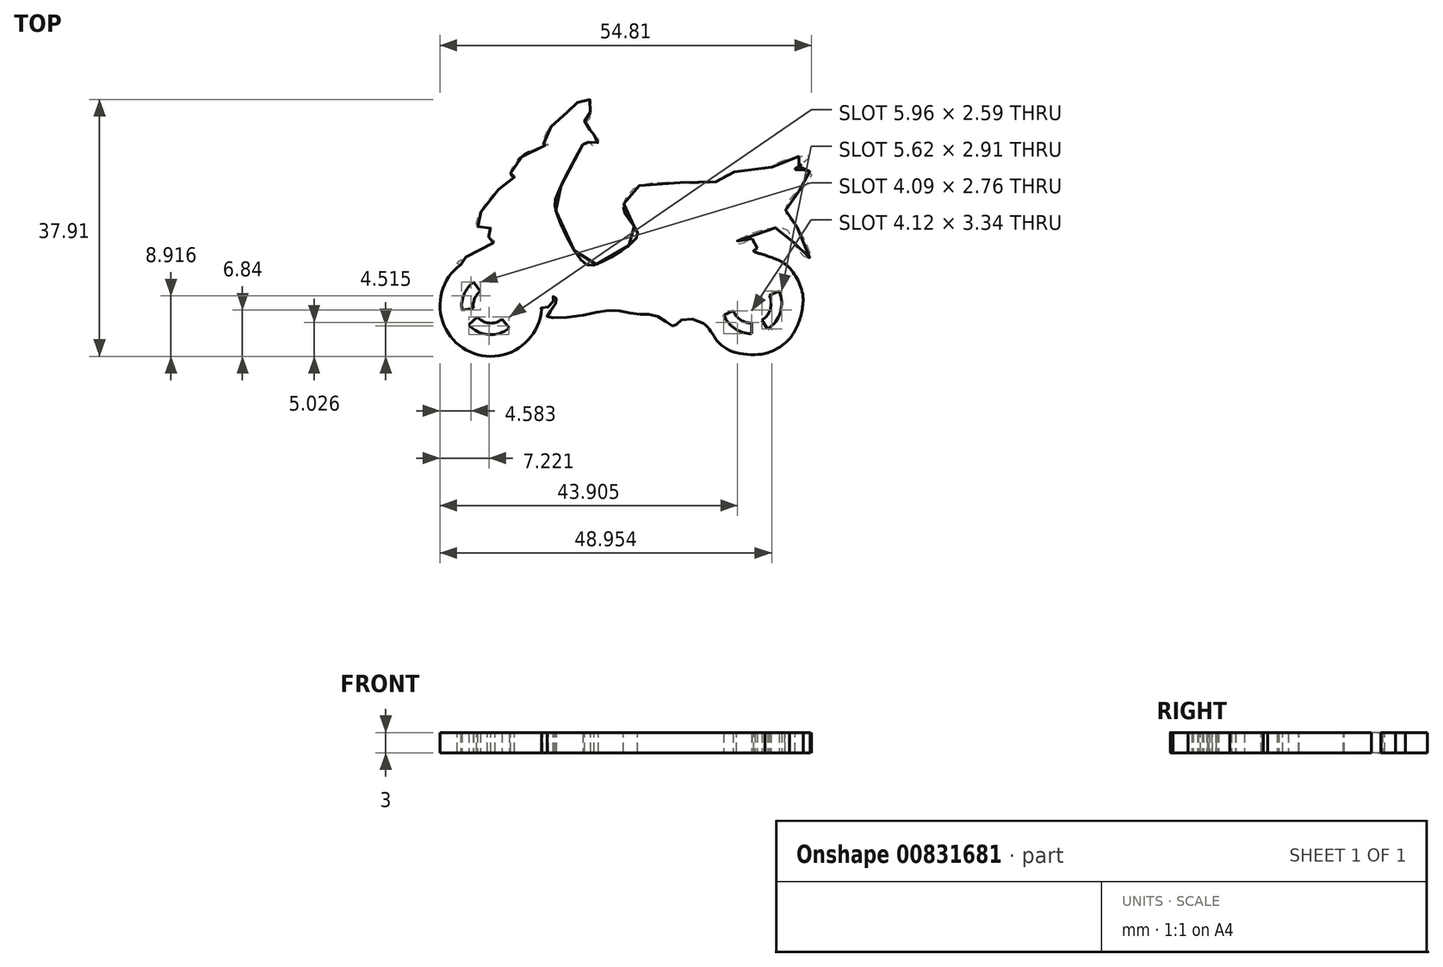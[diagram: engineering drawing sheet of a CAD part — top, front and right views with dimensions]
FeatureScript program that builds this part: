
annotation { "Feature Type Name" : "Feature", "Feature Type Description" : "" }
export const myFeature = defineFeature(function(context is Context, id is Id, definition is map)
    precondition{}
    {
        {
            var Q0;
            Q0=qCreatedBy(makeId("Top.planeOp"),FACE);
            var sketch = newSketch(context, id + "F0", { "sketchPlane" : qUnion([Q0])});
            skFitSpline(sketch, "E0", {"points": [v(13.76, 24.36) * mm, v(9.91, 16.67) * mm, v(9.86, 14.36) * mm, v(13.76, 6.98) * mm, v(15.97, 6.72) * mm, v(21.34, 10.1) * mm, v(21.76, 11.56) * mm, v(19.92, 14.3) * mm, v(20.18, 16.46) * mm, v(22.6, 18.41) * mm, v(30.77, 18.57) * mm, v(34.14, 19.15) * mm, v(35.35, 20.1) * mm, v(41.67, 20.94) * mm, v(42.09, 21.41) * mm, v(47.3, 22.57) * mm, v(45.14, 20.73) * mm, v(45.14, 20.62) * mm, v(47.35, 20.25) * mm, v(46.4, 17.99) * mm, v(44.25, 16.25) * mm, v(43.72, 13.99) * mm, v(44.83, 12.83) * mm, v(47.3, 7.83) * mm, v(46.83, 7.46) * mm, v(44.67, 10.3) * mm, v(43.2, 12.04) * mm, v(36.5, 10.04) * mm, v(36.61, 9.62) * mm, v(38.98, 10.56) * mm], "startDerivative": vector(-82.9, -156.15) * mm, "endDerivative": vector(91.63, 50.65) * mm});
            skFitSpline(sketch, "E1", {"points": [v(-4.24, 6.58) * mm, v(-4.76, 6.84) * mm, v(0.82, 9.98) * mm, v(0.55, 10.1) * mm, v(-0.29, 11.19) * mm, v(0.18, 11.91) * mm, v(-1.32, 12.04) * mm, v(-1.9, 12.64) * mm, v(1, 17.35) * mm, v(3.72, 19.55) * mm, v(3.5, 19.62) * mm, v(3.12, 19.93) * mm, v(5.41, 22.97) * mm, v(8.7, 24.31) * mm, v(8, 24.47) * mm, v(9.6, 27.5) * mm, v(12.35, 29.78) * mm, v(13.26, 30.69) * mm, v(14.86, 30.9) * mm, v(14.89, 30.5) * mm, v(14.54, 27.78) * mm, v(14.04, 27.74) * mm, v(14.2, 27.59) * mm, v(14.95, 26.34) * mm, v(15.42, 26.24) * mm, v(15.51, 25.55) * mm, v(16.05, 25.05) * mm, v(15.42, 24.11) * mm, v(14.57, 24.68) * mm, v(14.39, 24.36) * mm, v(13.76, 24.36) * mm], "startDerivative": vector(-43.04, 5.38) * mm, "endDerivative": vector(-33.57, 8.4) * mm});
            skArc(sketch, "E2", {"start": v(-4.24, 6.58) * mm, "mid": v(-3.34, -6.07) * mm, "end": v(7.68, 0.2) * mm});
            skPoint(sketch, "E2.third.point", {"position": v(-4.24, -5.5) * mm});
            skArc(sketch, "E3", {"start": v(31.58, -2.08) * mm, "mid": v(44.92, -3.58) * mm, "end": v(39.08, 8.5) * mm});
            skArc(sketch, "E4.0", {"start": v(-2.34, 4) * mm, "mid": v(-3.2, -2.08) * mm, "end": v(2.9, -2.8) * mm});
            skArc(sketch, "E5.0", {"start": v(-1.34, 2.63) * mm, "mid": v(-2.2, 1.54) * mm, "end": v(-2.37, 0.16) * mm});
            skLineSegment(sketch, "E6", {"start": v(-2.34, 4) * mm, "end": v(-1.34, 2.63) * mm});
            skLineSegment(sketch, "E7", {"start": v(4.46, 0) * mm, "end": v(2.74, 0) * mm});
            skLineSegment(sketch, "E8", {"start": v(0.2, 0.54) * mm, "end": v(2.9, -2.8) * mm});
            skLineSegment(sketch, "E9", {"start": v(0.2, 0.54) * mm, "end": v(-3.06, -2.26) * mm});
            skLineSegment(sketch, "E10", {"start": v(0.2, 0.54) * mm, "end": v(0.2, 0.54) * mm});
            skFitSpline(sketch, "E11.trimOffspring", {"points": [v(38.98, 10.56) * mm, v(39.48, 9.03) * mm, v(38.98, 8.6) * mm, v(43.53, 6.77) * mm, v(46.27, 1.34) * mm, v(44.38, -4.24) * mm, v(40.64, -6.56) * mm, v(34.37, -5.45) * mm, v(31.58, -2.08) * mm, v(28.1, -1.66) * mm, v(27.32, -2.5) * mm, v(26.53, -2.13) * mm, v(24.16, -0.82) * mm, v(21.73, -0.71) * mm, v(18.4, -0.14) * mm, v(13.65, -0.9) * mm, v(8.55, -1.14) * mm, v(8.57, -0.88) * mm, v(9.84, 1.02) * mm, v(9.84, 1.58) * mm, v(9.4, 1.91) * mm, v(9.47, 1.67) * mm, v(8.76, 0.35) * mm, v(7.62, 0.18) * mm, v(7.67, 0) * mm], "startDerivative": vector(30.19, -51.27) * mm, "endDerivative": vector(11.2, -17.98) * mm});
            skLineSegment(sketch, "E12", {"start": v(39.08, 8.5) * mm, "end": v(38.98, 8.6) * mm});
            skLineSegment(sketch, "E13", {"start": v(38.98, 8.6) * mm, "end": v(39.48, 9.03) * mm});
            skLineSegment(sketch, "E14", {"start": v(39.48, 9.03) * mm, "end": v(38.77, 10.45) * mm});
            skArc(sketch, "E15.0", {"start": v(-1.34, 2.63) * mm, "mid": v(-1.86, -1.05) * mm, "end": v(1.83, -1.48) * mm});
            skArc(sketch, "E16.0", {"start": v(34.55, -0.85) * mm, "mid": v(36.19, -2.86) * mm, "end": v(38.66, -3.6) * mm});
            skLineSegment(sketch, "E17", {"start": v(38.66, 0.85) * mm, "end": v(42.72, 2.7) * mm});
            skLineSegment(sketch, "E18", {"start": v(38.66, 0.85) * mm, "end": v(41.02, -2.93) * mm});
            skLineSegment(sketch, "E19", {"start": v(38.66, 0.85) * mm, "end": v(38.66, -3.6) * mm});
            skLineSegment(sketch, "E20", {"start": v(34.55, -0.85) * mm, "end": v(35.98, -0.26) * mm});
            skArc(sketch, "E21.0", {"start": v(35.98, -0.26) * mm, "mid": v(41.03, -0.83) * mm, "end": v(38.82, 3.75) * mm});
            skArc(sketch, "E22.trimOffspring", {"start": v(41.02, -2.93) * mm, "mid": v(42.98, 1.96) * mm, "end": v(38.9, 5.3) * mm});
            skLineSegment(sketch, "E23.trimOffspring", {"start": v(-2.37, 0.16) * mm, "end": v(-4.05, -0.09) * mm});
            skSolve(sketch);
        }
        {
            var Q0;
            {var subQ17=sQuery(id+"F0.wireOp",EDGE,"E1");Q0=makeQuery(id+"F0.imprint","IMPRINT",FACE,{"disambiguationData":[TD([[makeQuery(id+"F0.imprint","IMPRINT",EDGE,{"derivedFrom":subQ17}),-1.0]])]});}
            var Q1;
            {var subQ3=sQuery(id+"F0.wireOp",EDGE,"E23.trimOffspring");Q1=makeQuery(id+"F0.imprint","IMPRINT",FACE,{"disambiguationData":[TD([[makeQuery(id+"F0.imprint","IMPRINT",EDGE,{"derivedFrom":subQ3}),1.0]])]});}
            var Q2;
            {var subQ0=sQuery(id+"F0.wireOp",EDGE,"E15.0");var subQ1=sQuery(id+"F0.wireOp",EDGE,"E8");var subQ2=makeQuery(id+"F0.imprint","INTERSECT",VERTEX,{"derivedFrom":[subQ1,subQ0]});Q2=makeQuery(id+"F0.imprint","IMPRINT",FACE,{"disambiguationData":[TD([[makeQuery(id+"F0.imprint","IMPRINT",EDGE,{"disambiguationData":[TD([[subQ2,1.0]])],"derivedFrom":subQ1}),-1.0]])]});}
            var Q3;
            {var subQ1=sQuery(id+"F0.wireOp",EDGE,"E17");var subQ3=sQuery(id+"F0.wireOp",EDGE,"E21.0");var subQ4=makeQuery(id+"F0.imprint","INTERSECT",VERTEX,{"derivedFrom":[subQ1,subQ3]});Q3=makeQuery(id+"F0.imprint","IMPRINT",FACE,{"disambiguationData":[TD([[makeQuery(id+"F0.imprint","IMPRINT",EDGE,{"disambiguationData":[TD([[subQ4,1.0]])],"derivedFrom":subQ3}),1.0]])]});}
            var Q4;
            {var subQ0=sQuery(id+"F0.wireOp",EDGE,"E19");var subQ3=sQuery(id+"F0.wireOp",EDGE,"E21.0");var subQ5=makeQuery(id+"F0.imprint","INTERSECT",VERTEX,{"derivedFrom":[subQ0,subQ3]});Q4=makeQuery(id+"F0.imprint","IMPRINT",FACE,{"disambiguationData":[TD([[makeQuery(id+"F0.imprint","IMPRINT",EDGE,{"disambiguationData":[TD([[subQ5,-1.0]])],"derivedFrom":subQ3}),1.0]])]});}
            extrude(context, id + "F1", {"entities" : qUnion([Q0, Q1, Q2, Q3, Q4]), "depth" : 3 * mm, "offsetDistance" : 25 * mm});
        }
    });
